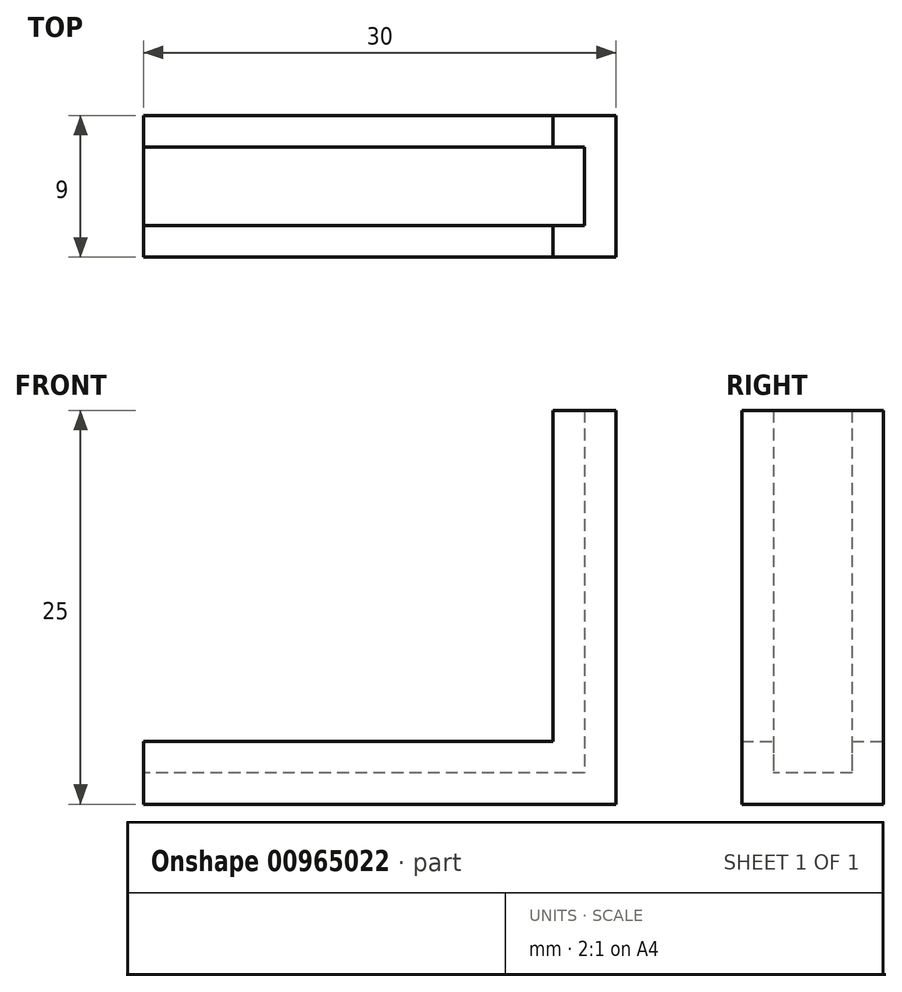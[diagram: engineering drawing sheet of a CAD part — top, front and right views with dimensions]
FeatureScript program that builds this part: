
annotation { "Feature Type Name" : "Feature", "Feature Type Description" : "" }
export const myFeature = defineFeature(function(context is Context, id is Id, definition is map)
    precondition{}
    {
        {
            var Q0;
            Q0=qCreatedBy(makeId("Top.planeOp"),FACE);
            var sketch = newSketch(context, id + "F0", { "sketchPlane" : qUnion([Q0])});
            skLineSegment(sketch, "E0.bottom", {"start": v(15, -4.5) * mm, "end": v(-15, -4.5) * mm});
            skLineSegment(sketch, "E0.top", {"start": v(15, 4.5) * mm, "end": v(-15, 4.5) * mm});
            skLineSegment(sketch, "E0.left", {"start": v(15, -4.5) * mm, "end": v(15, 4.5) * mm});
            skLineSegment(sketch, "E0.right", {"start": v(-15, -4.5) * mm, "end": v(-15, 4.5) * mm});
            skPoint(sketch, "E0.middle", {"position": v(0, 0) * mm});
            skPoint(sketch, "E1", {"position": v(-23.81, 2.5) * mm});
            skPoint(sketch, "E2", {"position": v(-13.6, -2.5) * mm});
            skLineSegment(sketch, "E3", {"start": v(-23.81, 2.5) * mm, "end": v(15, 2.5) * mm});
            skLineSegment(sketch, "E4", {"start": v(15, 2.5) * mm, "end": v(-15, 2.5) * mm});
            skLineSegment(sketch, "E5", {"start": v(-13.6, -2.5) * mm, "end": v(15, -2.5) * mm});
            skLineSegment(sketch, "E6", {"start": v(15, -2.5) * mm, "end": v(-15, -2.5) * mm});
            skLineSegment(sketch, "E7", {"start": v(11, 4.5) * mm, "end": v(11, -4.5) * mm});
            skLineSegment(sketch, "E8", {"start": v(13, -2.5) * mm, "end": v(13, 2.5) * mm});
            skSolve(sketch);
        }
        {
            var Q0;
            {var subQ0=sQuery(id+"F0.wireOp",EDGE,"E4");var subQ3=makeQuery(id+"F0.imprint","IMPRINT",VERTEX,{"derivedFrom":subQ0});Q0=makeQuery(id+"F0.imprint","IMPRINT",FACE,{"disambiguationData":[TD([[makeQuery(id+"F0.imprint","IMPRINT",EDGE,{"disambiguationData":[TD([[subQ3,1.0]])],"derivedFrom":subQ0}),1.0]])]});}
            var Q1;
            {var subQ1=sQuery(id+"F0.wireOp",EDGE,"E0.bottom");Q1=makeQuery(id+"F0.imprint","IMPRINT",FACE,{"disambiguationData":[TD([[makeQuery(id+"F0.imprint","IMPRINT",EDGE,{"derivedFrom":subQ1}),-1.0]])]});}
            var Q2;
            {var subQ5=sQuery(id+"F0.wireOp",EDGE,"E0.top");Q2=makeQuery(id+"F0.imprint","IMPRINT",FACE,{"disambiguationData":[TD([[makeQuery(id+"F0.imprint","IMPRINT",EDGE,{"derivedFrom":subQ5}),1.0]])]});}
            var Q3;
            {var subQ0=sQuery(id+"F0.wireOp",EDGE,"E6");var subQ3=makeQuery(id+"F0.imprint","IMPRINT",VERTEX,{"derivedFrom":subQ0});Q3=makeQuery(id+"F0.imprint","IMPRINT",FACE,{"disambiguationData":[TD([[makeQuery(id+"F0.imprint","IMPRINT",EDGE,{"disambiguationData":[TD([[subQ3,1.0]])],"derivedFrom":subQ0}),-1.0]])]});}
            var Q4;
            {var subQ0=sQuery(id+"F0.wireOp",EDGE,"E4");var subQ1=sQuery(id+"F0.wireOp",EDGE,"E0.left");var subQ2=makeQuery(id+"F0.imprint","INTERSECT",VERTEX,{"derivedFrom":[subQ1,subQ0]});Q4=makeQuery(id+"F0.imprint","IMPRINT",FACE,{"disambiguationData":[TD([[makeQuery(id+"F0.imprint","IMPRINT",EDGE,{"disambiguationData":[TD([[subQ2,1.0]])],"derivedFrom":subQ1}),1.0]])]});}
            var Q5;
            {var subQ0=sQuery(id+"F0.wireOp",EDGE,"E6");var subQ3=makeQuery(id+"F0.imprint","IMPRINT",VERTEX,{"derivedFrom":subQ0});Q5=makeQuery(id+"F0.imprint","IMPRINT",FACE,{"disambiguationData":[TD([[makeQuery(id+"F0.imprint","IMPRINT",EDGE,{"disambiguationData":[TD([[subQ3,1.0]])],"derivedFrom":subQ0}),1.0]])]});}
            var Q6;
            {var subQ0=sQuery(id+"F0.wireOp",EDGE,"E8");Q6=makeQuery(id+"F0.imprint","IMPRINT",FACE,{"disambiguationData":[TD([[makeQuery(id+"F0.imprint","IMPRINT",EDGE,{"derivedFrom":subQ0}),1.0]])]});}
            var Q7;
            {var subQ1=sQuery(id+"F0.wireOp",EDGE,"E0.left");var subQ6=sQuery(id+"F0.wireOp",EDGE,"E0.top");var subQ7=makeQuery(id+"F0.imprint","INTERSECT",VERTEX,{"derivedFrom":[subQ6,subQ1]});Q7=makeQuery(id+"F0.imprint","IMPRINT",FACE,{"disambiguationData":[TD([[makeQuery(id+"F0.imprint","IMPRINT",EDGE,{"disambiguationData":[TD([[subQ7,-1.0]])],"derivedFrom":subQ6}),1.0]])]});}
            extrude(context, id + "F1", {"entities" : qUnion([Q0, Q1, Q2, Q3, Q4, Q5, Q6, Q7]), "depth" : 2 * mm, "offsetDistance" : 25 * mm});
        }
        {
            var Q0;
            {var subQ1=sQuery(id+"F0.wireOp",EDGE,"E0.bottom");Q0=makeQuery(id+"F0.imprint","IMPRINT",FACE,{"disambiguationData":[TD([[makeQuery(id+"F0.imprint","IMPRINT",EDGE,{"derivedFrom":subQ1}),-1.0]])]});}
            var Q1;
            {var subQ5=sQuery(id+"F0.wireOp",EDGE,"E0.top");Q1=makeQuery(id+"F0.imprint","IMPRINT",FACE,{"disambiguationData":[TD([[makeQuery(id+"F0.imprint","IMPRINT",EDGE,{"derivedFrom":subQ5}),1.0]])]});}
            var Q2;
            {var subQ0=sQuery(id+"F0.wireOp",EDGE,"E6");var subQ3=makeQuery(id+"F0.imprint","IMPRINT",VERTEX,{"derivedFrom":subQ0});Q2=makeQuery(id+"F0.imprint","IMPRINT",FACE,{"disambiguationData":[TD([[makeQuery(id+"F0.imprint","IMPRINT",EDGE,{"disambiguationData":[TD([[subQ3,1.0]])],"derivedFrom":subQ0}),1.0]])]});}
            var Q3;
            {var subQ1=sQuery(id+"F0.wireOp",EDGE,"E0.left");var subQ6=sQuery(id+"F0.wireOp",EDGE,"E0.top");var subQ7=makeQuery(id+"F0.imprint","INTERSECT",VERTEX,{"derivedFrom":[subQ6,subQ1]});Q3=makeQuery(id+"F0.imprint","IMPRINT",FACE,{"disambiguationData":[TD([[makeQuery(id+"F0.imprint","IMPRINT",EDGE,{"disambiguationData":[TD([[subQ7,-1.0]])],"derivedFrom":subQ6}),1.0]])]});}
            extrude(context, id + "F2", {"entities" : qUnion([Q0, Q1, Q2, Q3]), "operationType" : NewBodyOperationType.ADD, "depth" : 4 * mm, "offsetDistance" : 25 * mm});
        }
        {
            var Q0;
            {var subQ5=sQuery(id+"F0.wireOp",EDGE,"E8");Q0=makeQuery(id+"F0.imprint","IMPRINT",FACE,{"disambiguationData":[TD([[makeQuery(id+"F0.imprint","IMPRINT",EDGE,{"derivedFrom":subQ5}),-1.0]])]});}
            var Q1;
            {var subQ1=sQuery(id+"F0.wireOp",EDGE,"E0.left");var subQ6=sQuery(id+"F0.wireOp",EDGE,"E0.bottom");var subQ7=makeQuery(id+"F0.imprint","INTERSECT",VERTEX,{"derivedFrom":[subQ6,subQ1]});Q1=makeQuery(id+"F0.imprint","IMPRINT",FACE,{"disambiguationData":[TD([[makeQuery(id+"F0.imprint","IMPRINT",EDGE,{"disambiguationData":[TD([[subQ7,-1.0]])],"derivedFrom":subQ6}),-1.0]])]});}
            var Q2;
            {var subQ1=sQuery(id+"F0.wireOp",EDGE,"E0.left");var subQ6=sQuery(id+"F0.wireOp",EDGE,"E0.top");var subQ7=makeQuery(id+"F0.imprint","INTERSECT",VERTEX,{"derivedFrom":[subQ6,subQ1]});Q2=makeQuery(id+"F0.imprint","IMPRINT",FACE,{"disambiguationData":[TD([[makeQuery(id+"F0.imprint","IMPRINT",EDGE,{"disambiguationData":[TD([[subQ7,-1.0]])],"derivedFrom":subQ6}),1.0]])]});}
            extrude(context, id + "F3", {"entities" : qUnion([Q0, Q1, Q2]), "operationType" : NewBodyOperationType.ADD, "depth" : 25 * mm, "offsetDistance" : 25 * mm});
        }
    });
